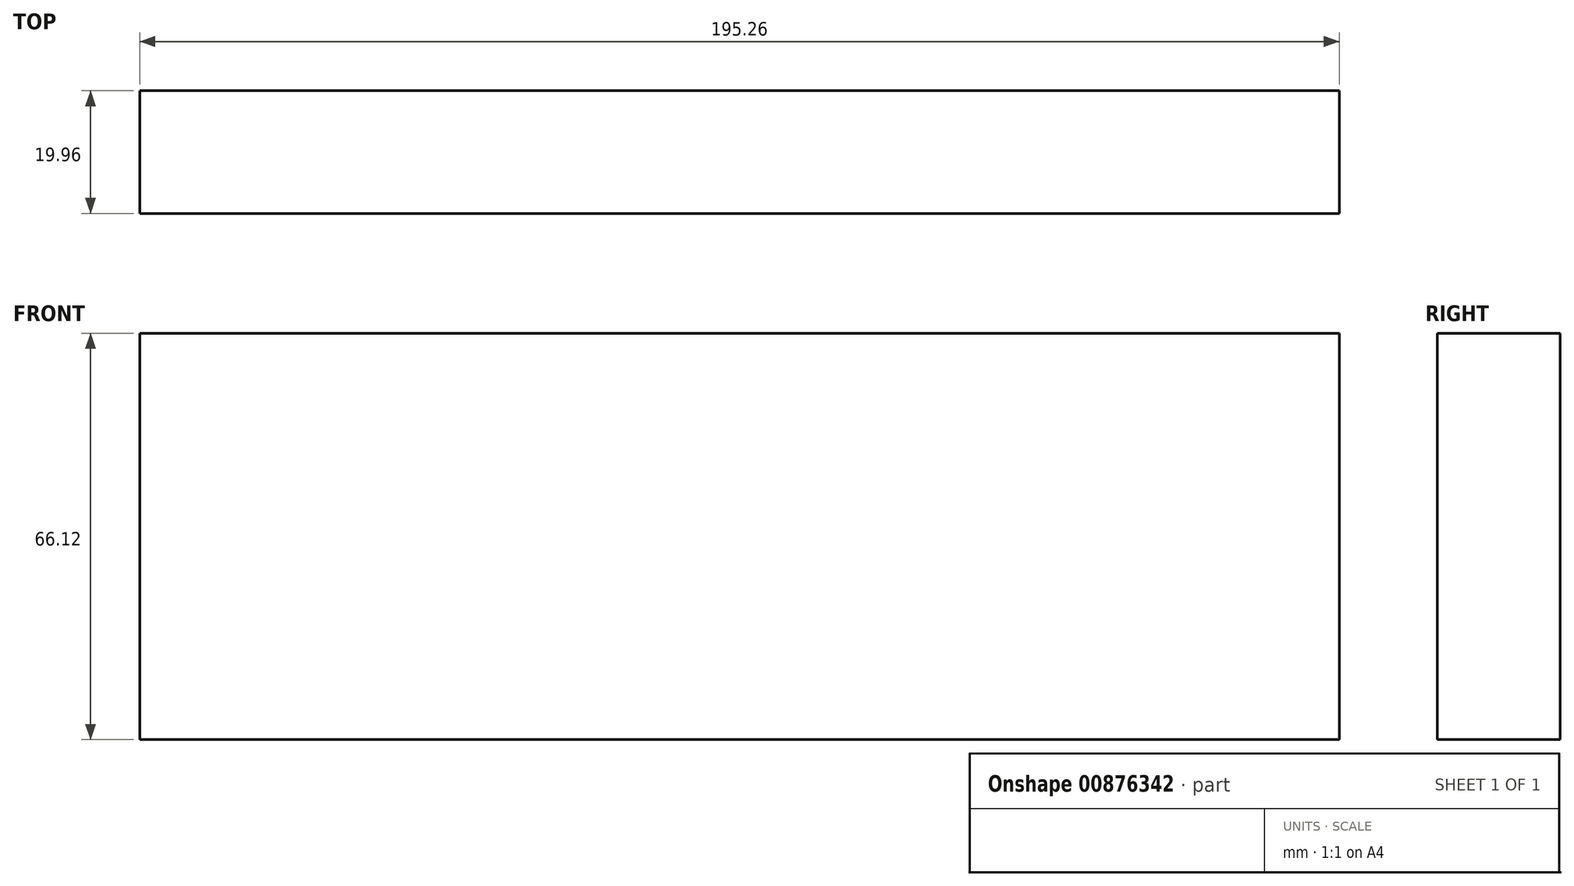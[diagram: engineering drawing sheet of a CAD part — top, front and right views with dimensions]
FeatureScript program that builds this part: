
annotation { "Feature Type Name" : "Feature", "Feature Type Description" : "" }
export const myFeature = defineFeature(function(context is Context, id is Id, definition is map)
    precondition{}
    {
        {
            var Q0;
            Q0=qCreatedBy(makeId("Front.planeOp"),FACE);
            var sketch = newSketch(context, id + "F0", { "sketchPlane" : qUnion([Q0])});
            skLineSegment(sketch, "E0.bottom", {"start": v(195.26, 66.12) * mm, "end": v(0, 66.12) * mm});
            skLineSegment(sketch, "E0.top", {"start": v(195.26, 0) * mm, "end": v(0, 0) * mm});
            skLineSegment(sketch, "E0.left", {"start": v(195.26, 66.12) * mm, "end": v(195.26, 0) * mm});
            skLineSegment(sketch, "E0.right", {"start": v(0, 66.12) * mm, "end": v(0, 0) * mm});
            skSolve(sketch);
        }
        {
            var Q0;
            Q0 = qSketchRegion(id + "F0", true);
            extrude(context, id + "F1", {"entities" : qUnion([Q0]), "depth" : 19.96 * mm, "offsetDistance" : 25.4 * mm});
        }
    });
